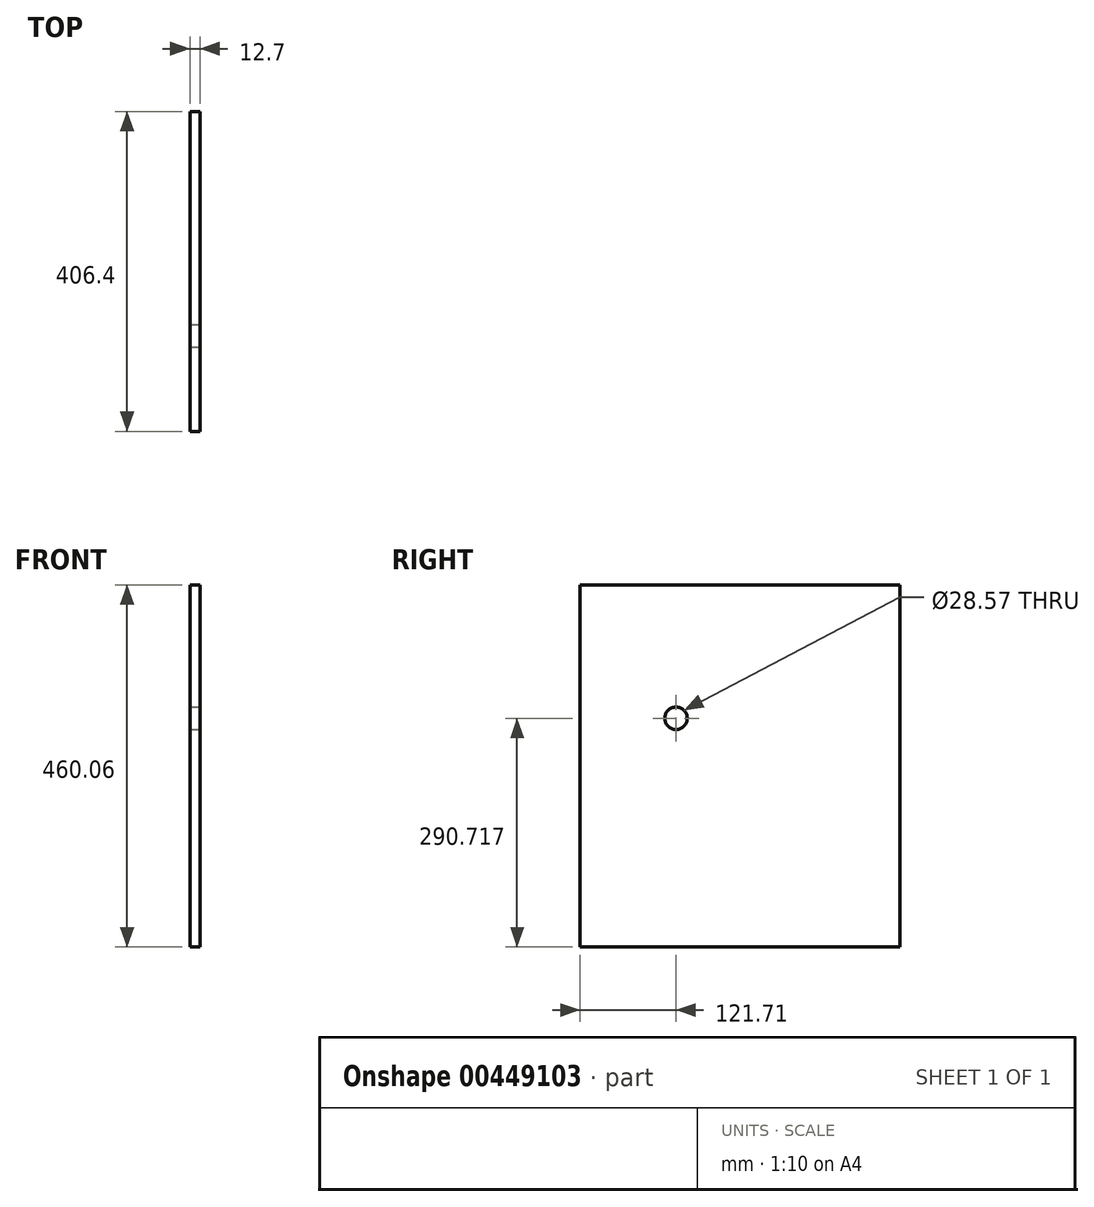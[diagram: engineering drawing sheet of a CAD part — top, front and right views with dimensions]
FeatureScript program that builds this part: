
annotation { "Feature Type Name" : "Feature", "Feature Type Description" : "" }
export const myFeature = defineFeature(function(context is Context, id is Id, definition is map)
    precondition{}
    {
        {
            var Q0;
            Q0=qCreatedBy(makeId("Right.planeOp"),FACE);
            var sketch = newSketch(context, id + "F0", { "sketchPlane" : qUnion([Q0])});
            skPoint(sketch, "E0.middle", {"position": v(-72.63, 33.23) * mm});
            skArc(sketch, "E1", {"start": v(-277.26, -171.4) * mm, "mid": v(-26.23, -41.1) * mm, "end": v(28.3, 236.43) * mm, "construction": true});
            skPoint(sketch, "E2.orphan", {"position": v(-286.96, 247.56) * mm});
            skPoint(sketch, "E0.left.start.orphan", {"position": v(132, 237.86) * mm});
            skPoint(sketch, "E0.top.start.orphan", {"position": v(141.7, -181.1) * mm});
            skLineSegment(sketch, "E3", {"start": v(0, 0) * mm, "end": v(-187.84, 92.88) * mm, "construction": true});
            skArc(sketch, "E4.0", {"start": v(-286.96, 38) * mm, "mid": v(-194.98, 83.17) * mm, "end": v(-174.48, 183.57) * mm, "construction": true});
            skLineSegment(sketch, "E5.bottom", {"start": v(-352.93, -171.4) * mm, "end": v(53.47, -171.4) * mm});
            skLineSegment(sketch, "E5.top", {"start": v(-352.93, 288.66) * mm, "end": v(53.47, 288.66) * mm});
            skLineSegment(sketch, "E5.left", {"start": v(-352.93, -171.4) * mm, "end": v(-352.93, 288.66) * mm});
            skLineSegment(sketch, "E5.right", {"start": v(53.47, -171.4) * mm, "end": v(53.47, 288.66) * mm});
            skSolve(sketch);
        }
        {
            var Q0;
            Q0=makeQuery(id+"F0.imprint","IMPRINT",FACE,{"disambiguationData":[TD([[makeQuery(id+"F0.imprint","IMPRINT",EDGE,{"derivedFrom":sQuery(id+"F0.wireOp",EDGE,"E5.bottom")}),1.0]])]});
            extrude(context, id + "F1", {"entities" : qUnion([Q0]), "depth" : 12.7 * mm});
        }
        {
            var Q0;
            Q0=makeQuery(id+"F1.opExtrude","CAP_FACE",FACE,{"disambiguationData":[OSD([sQuery(id+"F0.wireOp",EDGE,"E5.bottom"),sQuery(id+"F0.wireOp",EDGE,"E5.top"),sQuery(id+"F0.wireOp",EDGE,"E5.left"),sQuery(id+"F0.wireOp",EDGE,"E5.right")])],"isStart":false});
            var sketch = newSketch(context, id + "F2", { "sketchPlane" : qUnion([Q0])});
            skCircle(sketch, "E6", {"center": v(-231.22, 119.32) * mm, "radius": 50.8 * mm, "construction": true});
            skPoint(sketch, "E6.first.point", {"position": v(-187.84, 92.88) * mm});
            skPoint(sketch, "E6.second.point", {"position": v(-230.63, 68.52) * mm});
            skPoint(sketch, "E6.third.point", {"position": v(-183.24, 136) * mm});
            skCircle(sketch, "E7", {"center": v(-231.22, 119.32) * mm, "radius": 14.29 * mm});
            skSolve(sketch);
        }
        {
            var Q0;
            Q0=makeQuery(id+"F2.imprint","IMPRINT",FACE,{"disambiguationData":[TD([[makeQuery(id+"F2.imprint","IMPRINT",EDGE,{"derivedFrom":sQuery(id+"F2.wireOp",EDGE,"E7")}),1.0]])]});
            extrude(context, id + "F3", {"entities" : qUnion([Q0]), "operationType" : NewBodyOperationType.REMOVE, "endBound" : BoundingType.THROUGH_ALL, "oppositeDirection" : true, "depth" : 25.4 * mm});
        }
    });
